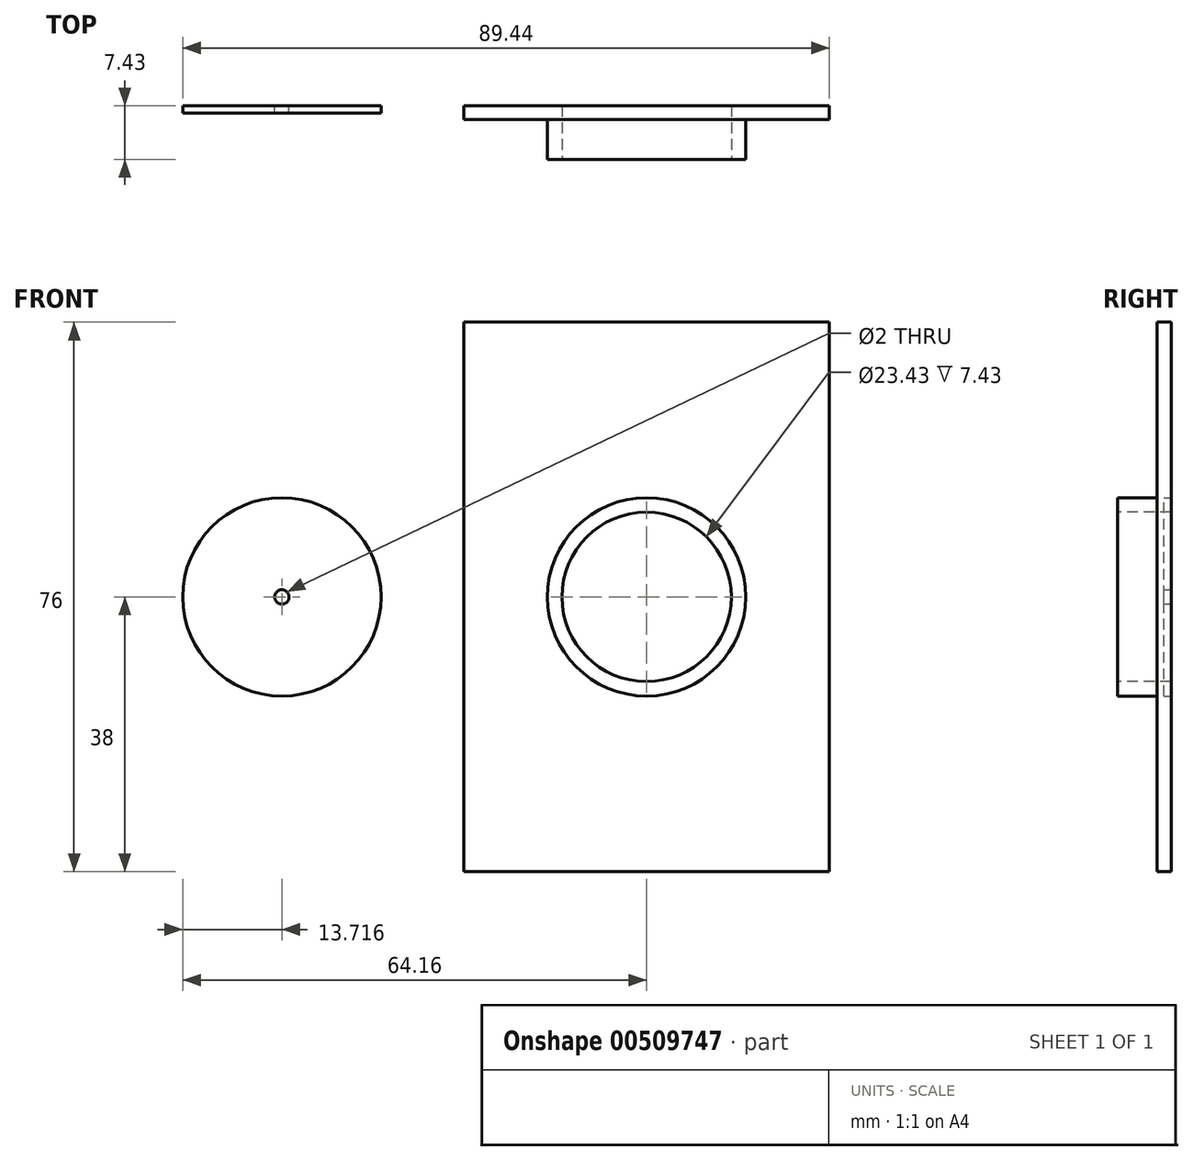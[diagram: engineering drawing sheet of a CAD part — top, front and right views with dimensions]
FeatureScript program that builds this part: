
annotation { "Feature Type Name" : "Feature", "Feature Type Description" : "" }
export const myFeature = defineFeature(function(context is Context, id is Id, definition is map)
    precondition{}
    {
        {
            var Q0;
            Q0=qCreatedBy(makeId("Front.planeOp"),FACE);
            var sketch = newSketch(context, id + "F0", { "sketchPlane" : qUnion([Q0])});
            skLineSegment(sketch, "E0.bottom", {"start": v(25.28, -38) * mm, "end": v(-25.28, -38) * mm});
            skLineSegment(sketch, "E0.top", {"start": v(25.28, 38) * mm, "end": v(-25.28, 38) * mm});
            skLineSegment(sketch, "E0.left", {"start": v(25.28, -38) * mm, "end": v(25.28, 38) * mm});
            skLineSegment(sketch, "E0.right", {"start": v(-25.28, -38) * mm, "end": v(-25.28, 38) * mm});
            skPoint(sketch, "E0.middle", {"position": v(0, 0) * mm});
            skSolve(sketch);
        }
        {
            var Q0;
            Q0=makeQuery(id+"F0.imprint","IMPRINT",FACE,{"disambiguationData":[TD([[makeQuery(id+"F0.imprint","IMPRINT",EDGE,{"derivedFrom":sQuery(id+"F0.wireOp",EDGE,"E0.bottom")}),-1.0]])]});
            extrude(context, id + "F1", {"entities" : qUnion([Q0]), "depth" : 1.93 * mm});
        }
        {
            var Q0;
            Q0=makeQuery(id+"F1.opExtrude","CAP_FACE",FACE,{"disambiguationData":[OSD([sQuery(id+"F0.wireOp",EDGE,"E0.bottom"),sQuery(id+"F0.wireOp",EDGE,"E0.top"),sQuery(id+"F0.wireOp",EDGE,"E0.left"),sQuery(id+"F0.wireOp",EDGE,"E0.right")])],"isStart":false});
            var sketch = newSketch(context, id + "F2", { "sketchPlane" : qUnion([Q0])});
            skCircle(sketch, "E1", {"center": v(0, 0) * mm, "radius": 11.71 * mm});
            skSolve(sketch);
        }
        {
            var Q0;
            Q0=makeQuery(id+"F2.imprint","IMPRINT",FACE,{"disambiguationData":[TD([[makeQuery(id+"F2.imprint","IMPRINT",EDGE,{"derivedFrom":sQuery(id+"F2.wireOp",EDGE,"E1")}),1.0]])]});
            extrude(context, id + "F3", {"entities" : qUnion([Q0]), "operationType" : NewBodyOperationType.REMOVE, "oppositeDirection" : true, "depth" : 1.93 * mm});
        }
        {
            var Q0;
            Q0=makeQuery(id+"F1.opExtrude","CAP_FACE",FACE,{"disambiguationData":[OSD([sQuery(id+"F0.wireOp",EDGE,"E0.bottom"),sQuery(id+"F0.wireOp",EDGE,"E0.top"),sQuery(id+"F0.wireOp",EDGE,"E0.left"),sQuery(id+"F0.wireOp",EDGE,"E0.right")])],"isStart":false});
            var sketch = newSketch(context, id + "F4", { "sketchPlane" : qUnion([Q0])});
            skCircle(sketch, "E2", {"center": v(0, 0) * mm, "radius": 11.71 * mm});
            skCircle(sketch, "E3", {"center": v(0, 0) * mm, "radius": 13.71 * mm});
            skSolve(sketch);
        }
        {
            var Q0;
            Q0=makeQuery(id+"F4.imprint","IMPRINT",FACE,{"disambiguationData":[TD([[makeQuery(id+"F4.imprint","IMPRINT",EDGE,{"derivedFrom":sQuery(id+"F4.wireOp",EDGE,"E2")}),-1.0]])]});
            extrude(context, id + "F5", {"entities" : qUnion([Q0]), "operationType" : NewBodyOperationType.ADD, "depth" : 5.5 * mm});
        }
        {
            var Q0;
            Q0=qCreatedBy(makeId("Front.planeOp"),FACE);
            var sketch = newSketch(context, id + "F6", { "sketchPlane" : qUnion([Q0])});
            skCircle(sketch, "E4", {"center": v(-50.44, 0) * mm, "radius": 13.71 * mm});
            skSolve(sketch);
        }
        {
            var Q0;
            Q0=makeQuery(id+"F6.imprint","IMPRINT",FACE,{"disambiguationData":[TD([[makeQuery(id+"F6.imprint","IMPRINT",EDGE,{"derivedFrom":sQuery(id+"F6.wireOp",EDGE,"E4")}),1.0]])]});
            extrude(context, id + "F7", {"entities" : qUnion([Q0]), "depth" : 1 * mm});
        }
        {
            var Q0;
            Q0=makeQuery(id+"F7.opExtrude","CAP_FACE",FACE,{"disambiguationData":[OSD([sQuery(id+"F6.wireOp",EDGE,"E4")])],"isStart":true});
            var sketch = newSketch(context, id + "F8", { "sketchPlane" : qUnion([Q0])});
            skLineSegment(sketch, "E5", {"start": v(36.73, 0) * mm, "end": v(64.16, 0) * mm, "construction": true});
            skPoint(sketch, "E6", {"position": v(50.44, 0) * mm});
            skSolve(sketch);
        }
        {
            var Q0;
            Q0=sQuery(id+"F8.wireOp",VERTEX,"E6");
            var Q1;
            Q1=makeQuery(id+"F7.opExtrude","SWEPT_BODY",BODY,{"disambiguationData":[OSD([sQuery(id+"F6.wireOp",EDGE,"E4")])]});
            hole(context, id + "F9", {"style" : HoleStyle.SIMPLE, "endStyle" : HoleEndStyle.THROUGH, "holeDiameter" : 2 * mm, "isTappedThrough" : true, "tappedDepth" : 12 * mm, "tapClearance" : 3, "startFromSketch" : true, "locations" : qUnion([Q0]), "scope" : qUnion([Q1])});
        }
    });
